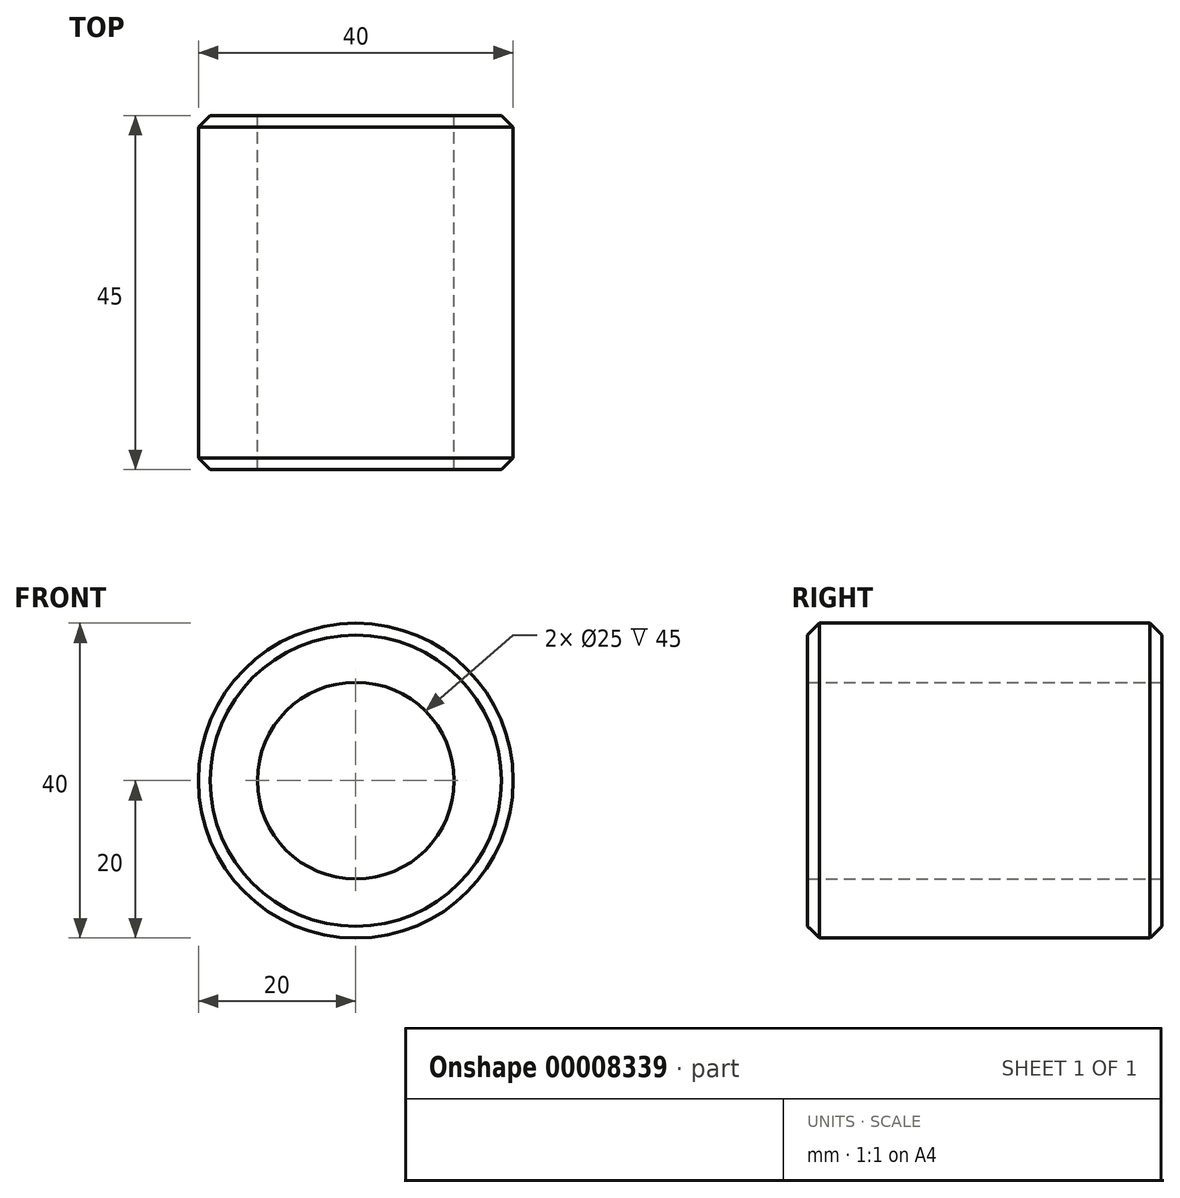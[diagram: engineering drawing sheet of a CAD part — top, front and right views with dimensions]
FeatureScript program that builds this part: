
annotation { "Feature Type Name" : "Feature", "Feature Type Description" : "" }
export const myFeature = defineFeature(function(context is Context, id is Id, definition is map)
    precondition{}
    {
        {
            var Q0;
            Q0=qCreatedBy(makeId("Front.planeOp"),FACE);
            var sketch = newSketch(context, id + "F0", { "sketchPlane" : qUnion([Q0])});
            skCircle(sketch, "E0", {"center": v(0, 0) * mm, "radius": 20 * mm});
            skCircle(sketch, "E1", {"center": v(0, 0) * mm, "radius": 12.5 * mm});
            skSolve(sketch);
        }
        {
            var Q0;
            Q0 = qSketchRegion(id + "F0", true);
            extrude(context, id + "F1", {"entities" : qUnion([Q0]), "depth" : 45 * mm});
        }
        {
            var Q0;
            Q0=makeQuery(id+"F1.opExtrude","CAP_EDGE",EDGE,{"disambiguationData":[OSD([sQuery(id+"F0.wireOp",EDGE,"E0")])],"isStart":false});
            chamfer(context, id + "F2", {"entities" : qUnion([Q0]), "width" : 1.5 * mm, "tangentPropagation" : true});
        }
        {
            var Q0;
            Q0=makeQuery(id+"F1.opExtrude","CAP_EDGE",EDGE,{"disambiguationData":[OSD([sQuery(id+"F0.wireOp",EDGE,"E0")])],"isStart":true});
            chamfer(context, id + "F3", {"entities" : qUnion([Q0]), "width" : 1.5 * mm, "tangentPropagation" : true});
        }
    });
